# Revit family: RN 80189 Optipress-Aquaplus-Valvola di ritegno EA
name_source: partatom
category: Rohrzubehör
units: mm (PartAtom-declared; Revit-internal decimal feet)

## family parameters
Arbeitsebenenbasiert = Nein
Beim Laden mit Abzugskörper schneiden = Nein
Bemaßung runder Anschluss = Durchmesser verwenden
Gemeinsam genutzt = Nein
Immer vertikal = Ja
Teiletyp = Ventil - Zerlegung in

## types (7) — shared parameters
1.010.00.2 Number of the part of the guideline = 17
1.010.00.3 Issue date (month) of the guideline = 201601
1.010.00.4 Manufacturer name = R. Nussbaum AG
1.010.00.5 Revision date of the file = 20190528
1.100.00.3 Sort number for display sequence = 4
1.100.00.4 Product designation = Rubinetti di sicurezza e a conduttura circolare
1.960/3L.00.8 Link (URL) = https://www.nussbaum.ch
17.700.00.4 valve assembly type = 6
17.700.00.7 maximum operating temperature TB [°C] = 90
17.700.00.8 maximum operating pressure(working pressure) ps [1.0 · 105 Pa] = 16
Connector Visibility = Nein
EnclosingSpace Visibility = Nein

## per-type parameters (varying)
| type | 1.800.00.3 BS number | 1.810.00.3 Manufacturer’s reference number | 1.810.00.4 DATANORM number | 1.810.00.5 StLB number | 1.810.00.6 GTIN number | 17.700.00.30 product description | 17.700.00.5 nominal size DN | 17.700.00.6 kvs-value [m3/h] | CONNECTOR0_DIAMETER_dX_0r | CONNECTOR0_dX_00 | CONNECTOR0_dX_01 | CONNECTOR0_ref_dX | CONNECTOR1_DIAMETER_dX_0r | CONNECTOR1_dX_00 | CONNECTOR1_dX_01 | CONNECTOR1_ref_dX | R. Nussbaum AG 80189.22 it Visibility | R. Nussbaum AG 80189.23 it Visibility | R. Nussbaum AG 80189.24 it Visibility | R. Nussbaum AG 80189.25 it Visibility | R. Nussbaum AG 80189.26 it Visibility | R. Nussbaum AG 80189.27 it Visibility | R. Nussbaum AG 80189.28 it Visibility |
| DN 12 | 0040320000000000000000000000090070000000000000000100000000 | 80189.22 | 80189.22 | 614.842 | 7612945737137 | 80189.22, Optipress-Aquaplus-Valvola di ritegno EA, DN=12 | 12 | 5.4 | 12 mm  [stored 0.0393701 ft] | 51 mm | 29 mm | 29 mm | 12 mm  [stored 0.0393701 ft] | 29 mm | 51 mm | 29 mm | Ja | Nein | Nein | Nein | Nein | Nein | Nein |
| DN 15 | 0040320000000000000000000000090070000000000000000200000000 | 80189.23 | 80189.23 | 614.843 | 7612945737144 | 80189.23, Optipress-Aquaplus-Valvola di ritegno EA, DN=15 | 15 | 5.4 | 15 mm  [stored 0.0492126 ft] | 55 mm | 33 mm | 33 mm | 15 mm  [stored 0.0492126 ft] | 33 mm | 55 mm | 33 mm | Nein | Ja | Nein | Nein | Nein | Nein | Nein |
| DN 20 | 0040320000000000000000000000090070000000000000000300000000 | 80189.24 | 80189.24 | 614.844 | 7612945737359 | 80189.24, Optipress-Aquaplus-Valvola di ritegno EA, DN=20 | 20 | 10.8 | 20 mm | 60 mm | 37 mm | 37 mm | 20 mm | 37 mm | 60 mm | 37 mm | Nein | Nein | Ja | Nein | Nein | Nein | Nein |
| DN 25 | 0040320000000000000000000000090070000000000000000400000000 | 80189.25 | 80189.25 | 614.845 | 7612945737519 | 80189.25, Optipress-Aquaplus-Valvola di ritegno EA, DN=25 | 25 | 16.8 | 25 mm  [stored 0.082021 ft] | 67 mm | 43 mm | 43 mm | 25 mm  [stored 0.082021 ft] | 43 mm | 67 mm | 43 mm | Nein | Nein | Nein | Ja | Nein | Nein | Nein |
| DN 32 | 0040320000000000000000000000090070000000000000000500000000 | 80189.26 | 80189.26 | 614.846 | 7612945735348 | 80189.26, Optipress-Aquaplus-Valvola di ritegno EA, DN=32 | 32 | 31.2 | 32 mm | 78 mm | 52 mm | 52 mm | 32 mm | 52 mm | 78 mm | 52 mm | Nein | Nein | Nein | Nein | Ja | Nein | Nein |
| DN 40 | 0040320000000000000000000000090070000000000000000600000000 | 80189.27 | 80189.27 | 614.847 | 7612945733719 | 80189.27, Optipress-Aquaplus-Valvola di ritegno EA, DN=40 | 40 | 45 | 40 mm | 93 mm | 57 mm | 57 mm | 40 mm | 57 mm | 93 mm | 57 mm | Nein | Nein | Nein | Nein | Nein | Ja | Nein |
| DN 50 | 0040320000000000000000000000090070000000000000000700000000 | 80189.28 | 80189.28 | 614.848 | 7612945734099 | 80189.28, Optipress-Aquaplus-Valvola di ritegno EA, DN=50 | 50 | 69 | 50 mm | 108 mm | 68 mm | 68 mm | 50 mm | 68 mm | 108 mm | 68 mm | Nein | Nein | Nein | Nein | Nein | Nein | Ja |

note: [stored X ft] marks values corroborated as IEEE doubles in the binary element streams (Revit-internal decimal feet)

## geometry (parser evidence)
native form markers: Sweep x2
no freeform markers — native parametric forms only
